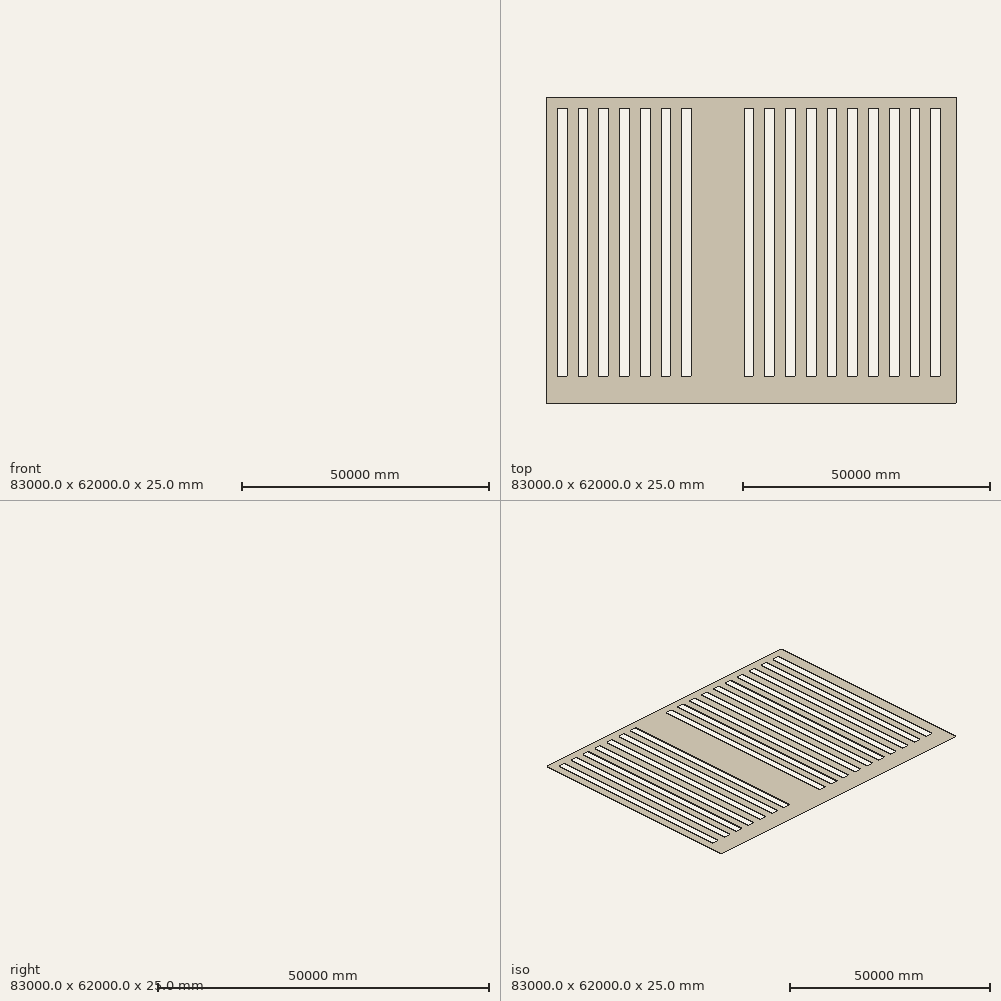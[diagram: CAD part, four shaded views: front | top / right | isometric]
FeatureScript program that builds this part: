
annotation { "Feature Type Name" : "Feature", "Feature Type Description" : "" }
export const myFeature = defineFeature(function(context is Context, id is Id, definition is map)
    precondition{}
    {
        {
            var Q0;
            Q0=qCreatedBy(makeId("Top.planeOp"),FACE);
            var sketch = newSketch(context, id + "F0", { "sketchPlane" : qUnion([Q0])});
            skLineSegment(sketch, "E0.bottom", {"start": v(-41500, 31000) * mm, "end": v(41500, 31000) * mm});
            skLineSegment(sketch, "E0.top", {"start": v(-41500, -31000) * mm, "end": v(41500, -31000) * mm});
            skLineSegment(sketch, "E0.left", {"start": v(-41500, 31000) * mm, "end": v(-41500, -31000) * mm});
            skLineSegment(sketch, "E0.right", {"start": v(41500, 31000) * mm, "end": v(41500, -31000) * mm});
            skPoint(sketch, "E0.middle", {"position": v(0, 0) * mm});
            skPoint(sketch, "E1", {"position": v(-39300, 28800) * mm});
            skPoint(sketch, "E2", {"position": v(-35100, 28800) * mm});
            skPoint(sketch, "E3", {"position": v(-30900, 28800) * mm});
            skPoint(sketch, "E4", {"position": v(-26700, 28800) * mm});
            skPoint(sketch, "E5", {"position": v(-22500, 28800) * mm});
            skPoint(sketch, "E6", {"position": v(-18300, 28800) * mm});
            skPoint(sketch, "E7", {"position": v(-14100, 28800) * mm});
            skPoint(sketch, "E8", {"position": v(-9900, 28800) * mm});
            skPoint(sketch, "E9", {"position": v(-5700, 28800) * mm});
            skPoint(sketch, "E10", {"position": v(-1500, 28800) * mm});
            skPoint(sketch, "E11", {"position": v(2700, 28800) * mm});
            skPoint(sketch, "E12", {"position": v(6900, 28800) * mm});
            skPoint(sketch, "E13", {"position": v(11100, 28800) * mm});
            skPoint(sketch, "E14", {"position": v(15300, 28800) * mm});
            skPoint(sketch, "E15", {"position": v(19500, 28800) * mm});
            skPoint(sketch, "E16", {"position": v(23700, 28800) * mm});
            skPoint(sketch, "E17", {"position": v(27900, 28800) * mm});
            skPoint(sketch, "E18", {"position": v(32100, 28800) * mm});
            skPoint(sketch, "E19", {"position": v(36300, 28800) * mm});
            skLineSegment(sketch, "E20", {"start": v(-39300, 28800) * mm, "end": v(-39300, -25600) * mm});
            skLineSegment(sketch, "E21", {"start": v(-39300, -25600) * mm, "end": v(-37300, -25600) * mm});
            skLineSegment(sketch, "E22", {"start": v(-37300, -25600) * mm, "end": v(-37300, 28800) * mm});
            skLineSegment(sketch, "E23", {"start": v(-37300, 28800) * mm, "end": v(-39300, 28800) * mm});
            skLineSegment(sketch, "E24", {"start": v(-35100, 28800) * mm, "end": v(-33100, 28800) * mm});
            skLineSegment(sketch, "E25", {"start": v(-33100, 28800) * mm, "end": v(-33100, -25600) * mm});
            skLineSegment(sketch, "E26", {"start": v(-33100, -25600) * mm, "end": v(-35100, -25600) * mm});
            skLineSegment(sketch, "E27", {"start": v(-35100, -25600) * mm, "end": v(-35100, 28800) * mm});
            skLineSegment(sketch, "E28.MirrorCS", {"start": v(-30900, 28800) * mm, "end": v(-30900, -25600) * mm});
            skLineSegment(sketch, "E29.MirrorCS", {"start": v(-28900, 28800) * mm, "end": v(-30900, 28800) * mm});
            skLineSegment(sketch, "E30.MirrorCS", {"start": v(-28900, -25600) * mm, "end": v(-28900, 28800) * mm});
            skLineSegment(sketch, "E31.MirrorCS", {"start": v(-26700, -25600) * mm, "end": v(-26700, 28800) * mm});
            skLineSegment(sketch, "E32.MirrorCS", {"start": v(-24700, 28800) * mm, "end": v(-24700, -25600) * mm});
            skLineSegment(sketch, "E33.MirrorCS", {"start": v(-26700, 28800) * mm, "end": v(-24700, 28800) * mm});
            skLineSegment(sketch, "E34.MirrorCS", {"start": v(-30900, -25600) * mm, "end": v(-28900, -25600) * mm});
            skLineSegment(sketch, "E35.MirrorCS", {"start": v(-24700, -25600) * mm, "end": v(-26700, -25600) * mm});
            skLineSegment(sketch, "E36.MirrorCS", {"start": v(-22500, 28800) * mm, "end": v(-22500, -25600) * mm});
            skLineSegment(sketch, "E37.MirrorCS", {"start": v(-20500, 28800) * mm, "end": v(-22500, 28800) * mm});
            skLineSegment(sketch, "E38.MirrorCS", {"start": v(-20500, -25600) * mm, "end": v(-20500, 28800) * mm});
            skLineSegment(sketch, "E39.MirrorCS", {"start": v(-18300, -25600) * mm, "end": v(-18300, 28800) * mm});
            skLineSegment(sketch, "E40.MirrorCS", {"start": v(-18300, 28800) * mm, "end": v(-16300, 28800) * mm});
            skLineSegment(sketch, "E41.MirrorCS", {"start": v(-16300, 28800) * mm, "end": v(-16300, -25600) * mm});
            skLineSegment(sketch, "E42.MirrorCS", {"start": v(-14100, 28800) * mm, "end": v(-14100, -25600) * mm});
            skLineSegment(sketch, "E43.MirrorCS", {"start": v(-12100, 28800) * mm, "end": v(-14100, 28800) * mm});
            skLineSegment(sketch, "E44.MirrorCS", {"start": v(-12100, -25600) * mm, "end": v(-12100, 28800) * mm});
            skLineSegment(sketch, "E45.MirrorCS", {"start": v(-9900, -25600) * mm, "end": v(-9900, 28800) * mm});
            skLineSegment(sketch, "E46.MirrorCS", {"start": v(-9873.65, 28800) * mm, "end": v(-7873.65, 28800) * mm});
            skLineSegment(sketch, "E47.MirrorCS", {"start": v(-7900, 28800) * mm, "end": v(-7900, -25600) * mm});
            skLineSegment(sketch, "E48.MirrorCS", {"start": v(-22500, -25600) * mm, "end": v(-20500, -25600) * mm});
            skLineSegment(sketch, "E49.MirrorCS", {"start": v(-16300, -25600) * mm, "end": v(-18300, -25600) * mm});
            skLineSegment(sketch, "E50.MirrorCS", {"start": v(-14100, -25600) * mm, "end": v(-12100, -25600) * mm});
            skLineSegment(sketch, "E51.MirrorCS", {"start": v(-7900, -25600) * mm, "end": v(-9900, -25600) * mm});
            skLineSegment(sketch, "E52.MirrorCS", {"start": v(-5700, 28800) * mm, "end": v(-5700, -25600) * mm});
            skLineSegment(sketch, "E53.MirrorCS", {"start": v(-3726.35, 28800) * mm, "end": v(-5726.35, 28800) * mm});
            skLineSegment(sketch, "E54.MirrorCS", {"start": v(-3700, -25600) * mm, "end": v(-3700, 28800) * mm});
            skLineSegment(sketch, "E55.MirrorCS", {"start": v(-1500, -25600) * mm, "end": v(-1500, 28800) * mm});
            skLineSegment(sketch, "E56.MirrorCS", {"start": v(-1500, 28800) * mm, "end": v(500, 28800) * mm});
            skLineSegment(sketch, "E57.MirrorCS", {"start": v(500, 28800) * mm, "end": v(500, -25600) * mm});
            skLineSegment(sketch, "E58.MirrorCS", {"start": v(2700, 28800) * mm, "end": v(2700, -25600) * mm});
            skLineSegment(sketch, "E59.MirrorCS", {"start": v(4700, 28800) * mm, "end": v(2700, 28800) * mm});
            skLineSegment(sketch, "E60.MirrorCS", {"start": v(4700, -25600) * mm, "end": v(4700, 28800) * mm});
            skLineSegment(sketch, "E61.MirrorCS", {"start": v(6900, 28800) * mm, "end": v(8900, 28800) * mm});
            skLineSegment(sketch, "E62.MirrorCS", {"start": v(6900, -25600) * mm, "end": v(6900, 28800) * mm});
            skLineSegment(sketch, "E63.MirrorCS", {"start": v(8900, 28800) * mm, "end": v(8900, -25600) * mm});
            skLineSegment(sketch, "E64.MirrorCS", {"start": v(11100, 28800) * mm, "end": v(11100, -25600) * mm});
            skLineSegment(sketch, "E65.MirrorCS", {"start": v(13100, 28800) * mm, "end": v(11100, 28800) * mm});
            skLineSegment(sketch, "E66.MirrorCS", {"start": v(13100, -25600) * mm, "end": v(13100, 28800) * mm});
            skLineSegment(sketch, "E67.MirrorCS", {"start": v(15300, -25600) * mm, "end": v(15300, 28800) * mm});
            skLineSegment(sketch, "E68.MirrorCS", {"start": v(15300, 28800) * mm, "end": v(17300, 28800) * mm});
            skLineSegment(sketch, "E69.MirrorCS", {"start": v(17300, 28800) * mm, "end": v(17300, -25600) * mm});
            skLineSegment(sketch, "E70.MirrorCS", {"start": v(19500, 28800) * mm, "end": v(19500, -25600) * mm});
            skLineSegment(sketch, "E71.MirrorCS", {"start": v(21500, 28800) * mm, "end": v(19500, 28800) * mm});
            skLineSegment(sketch, "E72.MirrorCS", {"start": v(21500, -25600) * mm, "end": v(21500, 28800) * mm});
            skLineSegment(sketch, "E73.MirrorCS", {"start": v(23700, -25600) * mm, "end": v(23700, 28800) * mm});
            skLineSegment(sketch, "E74.MirrorCS", {"start": v(23700, 28800) * mm, "end": v(25700, 28800) * mm});
            skLineSegment(sketch, "E75.MirrorCS", {"start": v(25700, 28800) * mm, "end": v(25700, -25600) * mm});
            skLineSegment(sketch, "E76.MirrorCS", {"start": v(27900, 28800) * mm, "end": v(27900, -25600) * mm});
            skLineSegment(sketch, "E77.MirrorCS", {"start": v(29900, 28800) * mm, "end": v(27900, 28800) * mm});
            skLineSegment(sketch, "E78.MirrorCS", {"start": v(29900, -25600) * mm, "end": v(29900, 28800) * mm});
            skLineSegment(sketch, "E79.MirrorCS", {"start": v(32100, -25600) * mm, "end": v(32100, 28800) * mm});
            skLineSegment(sketch, "E80.MirrorCS", {"start": v(32100, 28800) * mm, "end": v(34100, 28800) * mm});
            skLineSegment(sketch, "E81.MirrorCS", {"start": v(34100, 28800) * mm, "end": v(34100, -25600) * mm});
            skLineSegment(sketch, "E82.MirrorCS", {"start": v(36300, 28800) * mm, "end": v(36300, -25600) * mm});
            skLineSegment(sketch, "E83.MirrorCS", {"start": v(38300, 28800) * mm, "end": v(36300, 28800) * mm});
            skLineSegment(sketch, "E84.MirrorCS", {"start": v(38300, -25600) * mm, "end": v(38300, 28800) * mm});
            skLineSegment(sketch, "E85", {"start": v(-5700, -25600) * mm, "end": v(-3700, -25600) * mm});
            skLineSegment(sketch, "E86", {"start": v(-1500, -25600) * mm, "end": v(500, -25600) * mm});
            skLineSegment(sketch, "E87", {"start": v(2700, -25600) * mm, "end": v(4700, -25600) * mm});
            skLineSegment(sketch, "E88", {"start": v(6900, -25600) * mm, "end": v(8900, -25600) * mm});
            skLineSegment(sketch, "E89", {"start": v(11100, -25600) * mm, "end": v(13100, -25600) * mm});
            skLineSegment(sketch, "E90", {"start": v(15300, -25600) * mm, "end": v(17300, -25600) * mm});
            skLineSegment(sketch, "E91", {"start": v(19500, -25600) * mm, "end": v(21500, -25600) * mm});
            skLineSegment(sketch, "E92", {"start": v(23700, -25600) * mm, "end": v(25700, -25600) * mm});
            skLineSegment(sketch, "E93", {"start": v(27900, -25600) * mm, "end": v(29900, -25600) * mm});
            skLineSegment(sketch, "E94", {"start": v(32100, -25600) * mm, "end": v(34100, -25600) * mm});
            skLineSegment(sketch, "E95", {"start": v(36300, -25600) * mm, "end": v(38300, -25600) * mm});
            skSolve(sketch);
        }
        {
            var Q0;
            Q0=makeQuery(id+"F0.imprint","IMPRINT",FACE,{"disambiguationData":[TD([[makeQuery(id+"F0.imprint","IMPRINT",EDGE,{"derivedFrom":sQuery(id+"F0.wireOp",EDGE,"E0.bottom")}),-1.0]])]});
            extrude(context, id + "F1", {"entities" : qUnion([Q0]), "depth" : 25 * mm, "offsetDistance" : 25 * mm});
        }
        {
            var Q0;
            Q0=sQuery(id+"F0.wireOp",VERTEX,"E19");
            var Q1;
            Q1=sQuery(id+"F0.wireOp",VERTEX,"E18");
            var Q2;
            Q2=sQuery(id+"F0.wireOp",VERTEX,"E17");
            var Q3;
            Q3=sQuery(id+"F0.wireOp",VERTEX,"E16");
            var Q4;
            Q4=sQuery(id+"F0.wireOp",VERTEX,"E15");
            var Q5;
            Q5=sQuery(id+"F0.wireOp",VERTEX,"E14");
            var Q6;
            Q6=sQuery(id+"F0.wireOp",VERTEX,"E13");
            var Q7;
            Q7=sQuery(id+"F0.wireOp",VERTEX,"E12");
            var Q8;
            Q8=sQuery(id+"F0.wireOp",VERTEX,"E11");
            var Q9;
            Q9=sQuery(id+"F0.wireOp",VERTEX,"E10");
            var Q10;
            Q10=sQuery(id+"F0.wireOp",VERTEX,"E9");
            var Q11;
            Q11=sQuery(id+"F0.wireOp",VERTEX,"E8");
            var Q12;
            Q12=sQuery(id+"F0.wireOp",VERTEX,"E7");
            var Q13;
            Q13=sQuery(id+"F0.wireOp",VERTEX,"E6");
            var Q14;
            Q14=sQuery(id+"F0.wireOp",VERTEX,"E5");
            var Q15;
            Q15=sQuery(id+"F0.wireOp",VERTEX,"E4");
            var Q16;
            Q16=sQuery(id+"F0.wireOp",VERTEX,"E3");
            var Q17;
            Q17=sQuery(id+"F0.wireOp",VERTEX,"E2");
            var Q18;
            Q18=sQuery(id+"F0.wireOp",VERTEX,"E1");
            var Q19;
            Q19=makeQuery(id+"F1.opExtrude","SWEPT_BODY",BODY,{"disambiguationData":[OSD([sQuery(id+"F0.wireOp",EDGE,"E0.bottom"),sQuery(id+"F0.wireOp",EDGE,"E0.top"),sQuery(id+"F0.wireOp",EDGE,"E0.left"),sQuery(id+"F0.wireOp",EDGE,"E0.right")])]});
            hole(context, id + "F2", {"style" : HoleStyle.SIMPLE, "endStyle" : HoleEndStyle.BLIND, "oppositeDirection" : true, "holeDiameter" : 50 * mm, "majorDiameter" : 5 * mm, "holeDepth" : 50 * mm, "isTappedThrough" : true, "tappedDepth" : 12 * mm, "tapClearance" : 3, "startFromSketch" : true, "locations" : qUnion([Q0, Q1, Q2, Q3, Q4, Q5, Q6, Q7, Q8, Q9, Q10, Q11, Q12, Q13, Q14, Q15, Q16, Q17, Q18]), "scope" : qUnion([Q19])});
        }
    });
